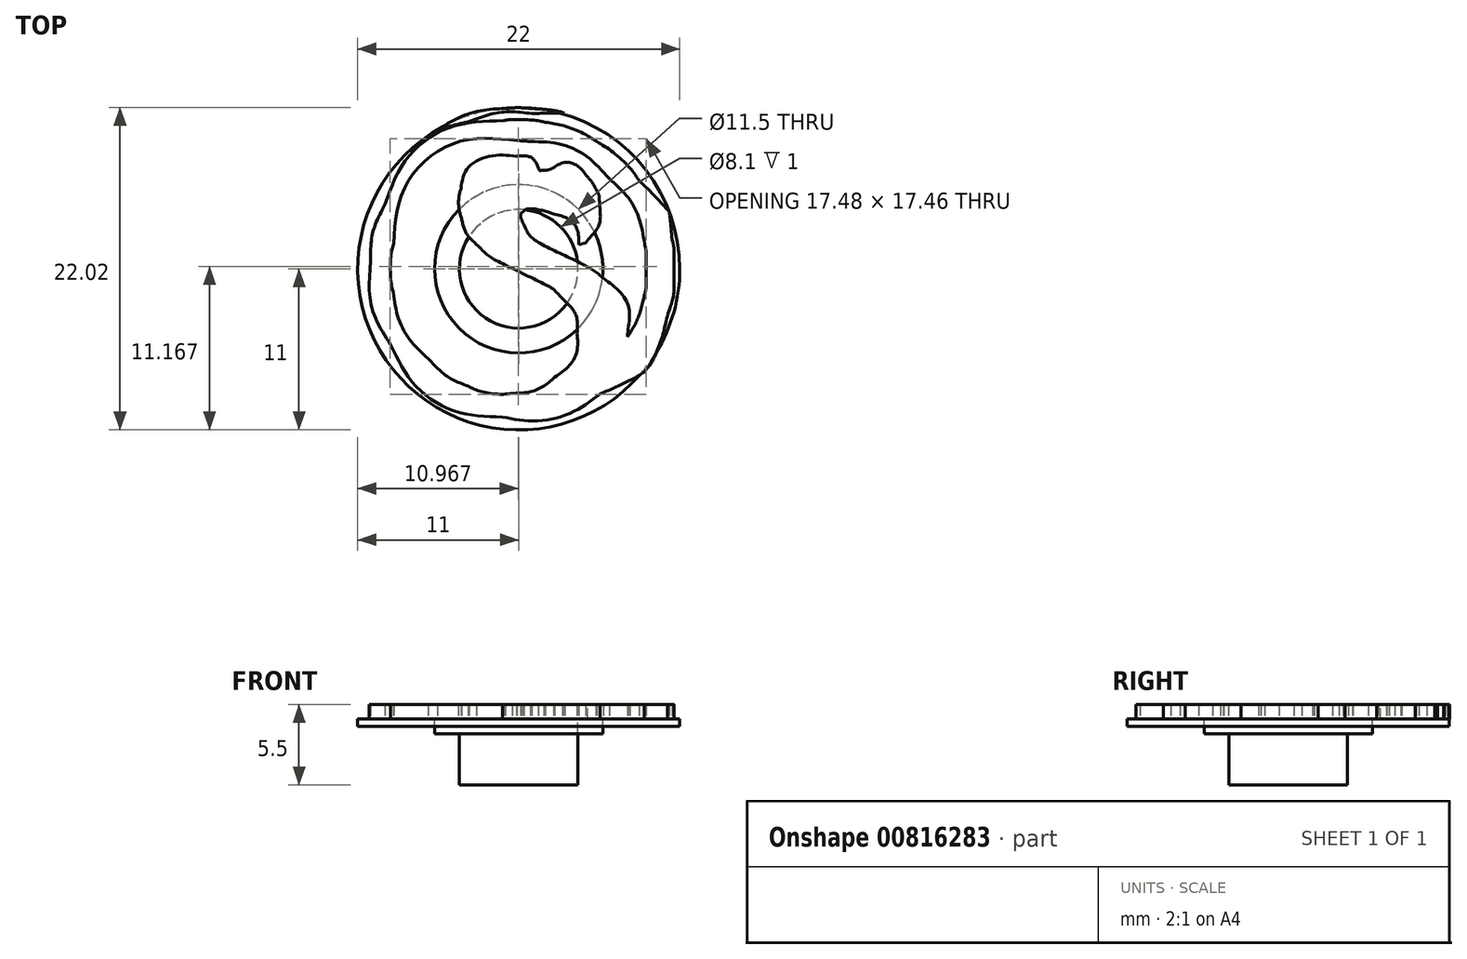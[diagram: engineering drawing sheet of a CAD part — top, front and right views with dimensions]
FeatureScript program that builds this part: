
annotation { "Feature Type Name" : "Feature", "Feature Type Description" : "" }
export const myFeature = defineFeature(function(context is Context, id is Id, definition is map)
    precondition{}
    {
        {
            var Q0;
            Q0=qCreatedBy(makeId("Top.planeOp"),FACE);
            var sketch = newSketch(context, id + "F0", { "sketchPlane" : qUnion([Q0])});
            skCircle(sketch, "E0", {"center": v(0, 0) * mm, "radius": 4.05 * mm});
            skCircle(sketch, "E1", {"center": v(0, 0) * mm, "radius": 5.75 * mm});
            skCircle(sketch, "E2", {"center": v(0, 0) * mm, "radius": 11 * mm});
            skSolve(sketch);
        }
        {
            var Q0;
            Q0=makeQuery(id+"F0.imprint","IMPRINT",FACE,{"disambiguationData":[TD([[makeQuery(id+"F0.imprint","IMPRINT",EDGE,{"derivedFrom":sQuery(id+"F0.wireOp",EDGE,"E0")}),-1.0]])]});
            extrude(context, id + "F1", {"entities" : qUnion([Q0]), "oppositeDirection" : true, "depth" : 1 * mm, "offsetDistance" : 25 * mm});
        }
        {
            var Q0;
            Q0=makeQuery(id+"F0.imprint","IMPRINT",FACE,{"disambiguationData":[TD([[makeQuery(id+"F0.imprint","IMPRINT",EDGE,{"derivedFrom":sQuery(id+"F0.wireOp",EDGE,"E1")}),-1.0]])]});
            extrude(context, id + "F2", {"entities" : qUnion([Q0]), "oppositeDirection" : true, "depth" : 0.5 * mm, "offsetDistance" : 25 * mm});
        }
        {
            var Q0;
            Q0=makeQuery(id+"F0.imprint","IMPRINT",FACE,{"disambiguationData":[TD([[makeQuery(id+"F0.imprint","IMPRINT",EDGE,{"derivedFrom":sQuery(id+"F0.wireOp",EDGE,"E0")}),1.0]])]});
            extrude(context, id + "F3", {"entities" : qUnion([Q0]), "oppositeDirection" : true, "depth" : 4.5 * mm, "offsetDistance" : 25 * mm});
        }
        {
            var Q0;
            Q0=makeQuery(id+"F3.opExtrude","CAP_FACE",FACE,{"disambiguationData":[OSD([sQuery(id+"F0.wireOp",EDGE,"E0")])],"isStart":true});
            var sketch = newSketch(context, id + "F4", { "sketchPlane" : qUnion([Q0])});
            skLineSegment(sketch, "E3", {"start": v(7.56, -4.44) * mm, "end": v(7.44, -4.63) * mm});
            skLineSegment(sketch, "E4", {"start": v(7.44, -4.63) * mm, "end": v(7.47, -4.1) * mm});
            skLineSegment(sketch, "E5", {"start": v(7.47, -4.1) * mm, "end": v(7.56, -4.44) * mm});
            skLineSegment(sketch, "E6", {"start": v(4.1, 1.64) * mm, "end": v(4.14, 1.26) * mm});
            skLineSegment(sketch, "E7", {"start": v(4.14, 1.26) * mm, "end": v(4.57, 1.8) * mm});
            skLineSegment(sketch, "E8", {"start": v(4.57, 1.8) * mm, "end": v(4.1, 1.64) * mm});
            skFitSpline(sketch, "E9", {"points": [v(-0.93, 10.95) * mm, v(-2.51, 10.82) * mm, v(-4.2, 10.27) * mm, v(-5.56, 9.46) * mm]});
            skFitSpline(sketch, "E10", {"points": [v(-5.56, 9.46) * mm, v(-9.07, 7.36) * mm, v(-11.1, 3.62) * mm, v(-10.95, -0.42) * mm]});
            skFitSpline(sketch, "E11", {"points": [v(-10.95, -0.42) * mm, v(-10.91, -1.53) * mm, v(-10.75, -2.45) * mm, v(-10.4, -3.46) * mm]});
            skFitSpline(sketch, "E12", {"points": [v(-10.4, -3.46) * mm, v(-9.46, -6.32) * mm, v(-7.43, -8.62) * mm, v(-4.73, -9.92) * mm]});
            skFitSpline(sketch, "E13", {"points": [v(-4.73, -9.92) * mm, v(1.4, -12.85) * mm, v(8.7, -9.58) * mm, v(10.58, -3.04) * mm]});
            skFitSpline(sketch, "E14", {"points": [v(10.58, -3.04) * mm, v(10.9, -1.92) * mm, v(10.96, -1.5) * mm, v(10.96, 0.03) * mm]});
            skFitSpline(sketch, "E15", {"points": [v(10.96, 0.03) * mm, v(10.96, 1.31) * mm, v(10.95, 1.48) * mm, v(10.8, 2.17) * mm]});
            skFitSpline(sketch, "E16", {"points": [v(10.8, 2.17) * mm, v(10.07, 5.61) * mm, v(7.88, 8.4) * mm, v(4.75, 9.91) * mm]});
            skFitSpline(sketch, "E17", {"points": [v(4.75, 9.91) * mm, v(3.5, 10.5) * mm, v(2.3, 10.83) * mm, v(0.81, 10.95) * mm]});
            skFitSpline(sketch, "E18", {"points": [v(0.81, 10.95) * mm, v(-0.02, 11.02) * mm, v(-0.04, 11.02) * mm, v(-0.93, 10.95) * mm]});
            skFitSpline(sketch, "E19", {"points": [v(0.9, 10.6) * mm, v(5.64, 10.17) * mm, v(9.44, 6.78) * mm, v(10.47, 2.05) * mm]});
            skFitSpline(sketch, "E20", {"points": [v(10.47, 2.05) * mm, v(10.59, 1.5) * mm, v(10.6, 1.26) * mm, v(10.6, 0) * mm]});
            skFitSpline(sketch, "E21", {"points": [v(10.6, 0) * mm, v(10.6, -1.57) * mm, v(10.54, -2.01) * mm, v(10.15, -3.22) * mm]});
            skFitSpline(sketch, "E22", {"points": [v(10.15, -3.22) * mm, v(9.27, -6) * mm, v(7.28, -8.29) * mm, v(4.67, -9.56) * mm]});
            skFitSpline(sketch, "E23", {"points": [v(4.67, -9.56) * mm, v(0.18, -11.76) * mm, v(-5.17, -10.54) * mm, v(-8.3, -6.61) * mm]});
            skFitSpline(sketch, "E24", {"points": [v(-8.3, -6.61) * mm, v(-9.36, -5.3) * mm, v(-10.05, -3.8) * mm, v(-10.42, -2.06) * mm]});
            skFitSpline(sketch, "E25", {"points": [v(-10.42, -2.06) * mm, v(-10.56, -1.38) * mm, v(-10.58, -1.18) * mm, v(-10.58, -0.06) * mm]});
            skFitSpline(sketch, "E26", {"points": [v(-10.58, -0.06) * mm, v(-10.59, 1.28) * mm, v(-10.5, 1.87) * mm, v(-10.22, 2.88) * mm]});
            skFitSpline(sketch, "E27", {"points": [v(-10.22, 2.88) * mm, v(-9.25, 6.26) * mm, v(-6.7, 8.93) * mm, v(-3.4, 10.06) * mm]});
            skFitSpline(sketch, "E28", {"points": [v(-3.4, 10.06) * mm, v(-1.94, 10.55) * mm, v(-0.57, 10.73) * mm, v(0.9, 10.6) * mm]});
            skFitSpline(sketch, "E29", {"points": [v(-1.06, 10.12) * mm, v(-4.64, 9.68) * mm, v(-7.6, 7.58) * mm, v(-9.14, 4.4) * mm]});
            skFitSpline(sketch, "E30", {"points": [v(-9.14, 4.4) * mm, v(-9.8, 3.03) * mm, v(-10.07, 1.91) * mm, v(-10.12, 0.4) * mm]});
            skFitSpline(sketch, "E31", {"points": [v(-10.12, 0.4) * mm, v(-10.2, -1.68) * mm, v(-9.76, -3.44) * mm, v(-8.75, -5.17) * mm]});
            skFitSpline(sketch, "E32", {"points": [v(-8.75, -5.17) * mm, v(-7.14, -7.9) * mm, v(-4.33, -9.72) * mm, v(-1.12, -10.12) * mm]});
            skFitSpline(sketch, "E33", {"points": [v(-1.12, -10.12) * mm, v(1.12, -10.4) * mm, v(3.64, -9.8) * mm, v(5.56, -8.54) * mm]});
            skFitSpline(sketch, "E34", {"points": [v(5.56, -8.54) * mm, v(10.48, -5.3) * mm, v(11.68, 1.27) * mm, v(8.21, 6.02) * mm]});
            skFitSpline(sketch, "E35", {"points": [v(8.21, 6.02) * mm, v(7.55, 6.93) * mm, v(6.34, 8.04) * mm, v(5.32, 8.68) * mm]});
            skFitSpline(sketch, "E36", {"points": [v(5.32, 8.68) * mm, v(4.4, 9.26) * mm, v(3, 9.79) * mm, v(1.82, 10) * mm]});
            skFitSpline(sketch, "E37", {"points": [v(1.82, 10) * mm, v(1.07, 10.14) * mm, v(-0.39, 10.2) * mm, v(-1.06, 10.12) * mm]});
            skFitSpline(sketch, "E38", {"points": [v(0.81, 8.7) * mm, v(2.87, 8.5) * mm, v(4.7, 7.64) * mm, v(6.2, 6.15) * mm]});
            skFitSpline(sketch, "E39", {"points": [v(6.2, 6.15) * mm, v(7.45, 4.88) * mm, v(8.21, 3.48) * mm, v(8.6, 1.68) * mm]});
            skFitSpline(sketch, "E40", {"points": [v(8.6, 1.68) * mm, v(8.68, 1.3) * mm, v(8.7, 0.92) * mm, v(8.7, -0.06) * mm]});
            skFitSpline(sketch, "E41", {"points": [v(8.7, -0.06) * mm, v(8.7, -1.17) * mm, v(8.69, -1.37) * mm, v(8.56, -1.87) * mm]});
            skFitSpline(sketch, "E42", {"points": [v(8.56, -1.87) * mm, v(8.32, -2.85) * mm, v(7.97, -3.76) * mm, v(7.56, -4.44) * mm]});
            skFitSpline(sketch, "E43", {"points": [v(7.47, -4.1) * mm, v(7.55, -2.8) * mm, v(6.99, -1.66) * mm, v(5.77, -0.65) * mm]});
            skFitSpline(sketch, "E44", {"points": [v(5.77, -0.65) * mm, v(5.23, -0.2) * mm, v(4.43, 0.28) * mm, v(3.16, 0.9) * mm]});
            skFitSpline(sketch, "E45", {"points": [v(3.16, 0.9) * mm, v(1.55, 1.7) * mm, v(0.71, 2.33) * mm, v(0.37, 3) * mm]});
            skFitSpline(sketch, "E46", {"points": [v(0.37, 3) * mm, v(0.18, 3.4) * mm, v(0.14, 3.77) * mm, v(0.27, 3.88) * mm]});
            skFitSpline(sketch, "E47", {"points": [v(0.27, 3.88) * mm, v(0.5, 4.08) * mm, v(1.54, 4) * mm, v(2.4, 3.73) * mm]});
            skFitSpline(sketch, "E48", {"points": [v(2.4, 3.73) * mm, v(3.38, 3.42) * mm, v(4, 2.68) * mm, v(4.1, 1.64) * mm]});
            skFitSpline(sketch, "E49", {"points": [v(4.57, 1.8) * mm, v(5.34, 2.72) * mm, v(5.57, 3.34) * mm, v(5.52, 4.4) * mm]});
            skFitSpline(sketch, "E50", {"points": [v(5.52, 4.4) * mm, v(5.5, 4.96) * mm, v(5.47, 5.05) * mm, v(5.28, 5.45) * mm]});
            skFitSpline(sketch, "E51", {"points": [v(5.28, 5.45) * mm, v(5.15, 5.7) * mm, v(4.9, 6.05) * mm, v(4.7, 6.28) * mm]});
            skFitSpline(sketch, "E52", {"points": [v(4.7, 6.28) * mm, v(4, 7.04) * mm, v(3.16, 7.27) * mm, v(2.37, 6.9) * mm]});
            skFitSpline(sketch, "E53", {"points": [v(2.37, 6.9) * mm, v(2.18, 6.81) * mm, v(1.9, 6.74) * mm, v(1.73, 6.73) * mm]});
            skFitSpline(sketch, "E54", {"points": [v(1.73, 6.73) * mm, v(1.44, 6.71) * mm, v(1.42, 6.72) * mm, v(1.33, 6.9) * mm]});
            skFitSpline(sketch, "E55", {"points": [v(1.33, 6.9) * mm, v(1.05, 7.45) * mm, v(0.58, 7.7) * mm, v(-0.15, 7.7) * mm]});
            skFitSpline(sketch, "E56", {"points": [v(-0.15, 7.7) * mm, v(-2.06, 7.68) * mm, v(-3.55, 6.8) * mm, v(-3.94, 5.45) * mm]});
            skFitSpline(sketch, "E57", {"points": [v(-3.94, 5.45) * mm, v(-4.09, 4.97) * mm, v(-4.07, 4.06) * mm, v(-3.91, 3.45) * mm]});
            skFitSpline(sketch, "E58", {"points": [v(-3.91, 3.45) * mm, v(-3.72, 2.74) * mm, v(-3.42, 2.2) * mm, v(-2.87, 1.66) * mm]});
            skFitSpline(sketch, "E59", {"points": [v(-2.87, 1.66) * mm, v(-2.22, 1) * mm, v(-1.52, 0.57) * mm, v(0.25, -0.3) * mm]});
            skFitSpline(sketch, "E60", {"points": [v(0.25, -0.3) * mm, v(2, -1.17) * mm, v(2.4, -1.43) * mm, v(3, -2.04) * mm]});
            skFitSpline(sketch, "E61", {"points": [v(3, -2.04) * mm, v(3.7, -2.79) * mm, v(3.99, -3.47) * mm, v(3.99, -4.41) * mm]});
            skFitSpline(sketch, "E62", {"points": [v(3.99, -4.41) * mm, v(3.99, -5.59) * mm, v(3.47, -6.6) * mm, v(2.46, -7.4) * mm]});
            skFitSpline(sketch, "E63", {"points": [v(2.46, -7.4) * mm, v(1.64, -8.05) * mm, v(0.67, -8.42) * mm, v(-0.43, -8.5) * mm]});
            skFitSpline(sketch, "E64", {"points": [v(-0.43, -8.5) * mm, v(-1.35, -8.56) * mm, v(-2.67, -8.35) * mm, v(-3.45, -8.02) * mm]});
            skFitSpline(sketch, "E65", {"points": [v(-3.45, -8.02) * mm, v(-4.5, -7.56) * mm, v(-5.32, -7) * mm, v(-6.2, -6.12) * mm]});
            skFitSpline(sketch, "E66", {"points": [v(-6.2, -6.12) * mm, v(-7.42, -4.89) * mm, v(-8.22, -3.36) * mm, v(-8.58, -1.6) * mm]});
            skFitSpline(sketch, "E67", {"points": [v(-8.58, -1.6) * mm, v(-8.74, -0.8) * mm, v(-8.73, 0.91) * mm, v(-8.55, 1.73) * mm]});
            skFitSpline(sketch, "E68", {"points": [v(-8.55, 1.73) * mm, v(-7.67, 5.79) * mm, v(-4.26, 8.62) * mm, v(-0.1, 8.75) * mm]});
            skFitSpline(sketch, "E69", {"points": [v(-0.1, 8.75) * mm, v(0.04, 8.75) * mm, v(0.46, 8.73) * mm, v(0.81, 8.7) * mm]});
            skFitSpline(sketch, "E70", {"points": [v(-7.18, -0.9) * mm, v(-7.67, -0.93) * mm, v(-7.65, -0.9) * mm, v(-7.46, -1.8) * mm]});
            skFitSpline(sketch, "E71", {"points": [v(-7.46, -1.8) * mm, v(-6.76, -5.1) * mm, v(-3.86, -7.57) * mm, v(-0.68, -7.58) * mm]});
            skFitSpline(sketch, "E72", {"points": [v(-0.68, -7.58) * mm, v(0.73, -7.59) * mm, v(1.55, -7.17) * mm, v(2.04, -6.16) * mm]});
            skFitSpline(sketch, "E73", {"points": [v(2.04, -6.16) * mm, v(2.23, -5.78) * mm, v(2.24, -5.73) * mm, v(2.24, -5.08) * mm]});
            skFitSpline(sketch, "E74", {"points": [v(2.24, -5.08) * mm, v(2.24, -4.44) * mm, v(2.22, -4.37) * mm, v(2.05, -4) * mm]});
            skFitSpline(sketch, "E75", {"points": [v(2.05, -4) * mm, v(1.66, -3.18) * mm, v(0.97, -2.56) * mm, v(-0.14, -2.02) * mm]});
            skFitSpline(sketch, "E76", {"points": [v(-0.14, -2.02) * mm, v(-1.14, -1.53) * mm, v(-2.26, -1.2) * mm, v(-3.56, -1) * mm]});
            skFitSpline(sketch, "E77", {"points": [v(-3.56, -1) * mm, v(-4.17, -0.92) * mm, v(-6.38, -0.85) * mm, v(-7.18, -0.9) * mm]});
            skSolve(sketch);
        }
        {
            var Q0;
            Q0=makeQuery(id+"F4.imprint","IMPRINT",FACE,{"disambiguationData":[TD([[makeQuery(id+"F4.imprint","IMPRINT",EDGE,{"derivedFrom":sQuery(id+"F4.wireOp",EDGE,"E8")}),-1.0]])]});
            var Q1;
            {var subQ4=sQuery(id+"F4.wireOp",EDGE,"E45");Q1=makeQuery(id+"F4.imprint","IMPRINT",FACE,{"disambiguationData":[TD([[makeQuery(id+"F4.imprint","IMPRINT",EDGE,{"derivedFrom":subQ4}),1.0]])]});}
            var Q2;
            Q2=makeQuery(id+"F4.imprint","IMPRINT",FACE,{"disambiguationData":[TD([[makeQuery(id+"F4.imprint","IMPRINT",EDGE,{"derivedFrom":sQuery(id+"F4.wireOp",EDGE,"E3")}),1.0]])]});
            var Q3;
            Q3=makeQuery(id+"F4.imprint","IMPRINT",FACE,{"disambiguationData":[TD([[makeQuery(id+"F4.imprint","IMPRINT",EDGE,{"derivedFrom":sQuery(id+"F4.wireOp",EDGE,"E9")}),1.0]])]});
            extrude(context, id + "F5", {"entities" : qUnion([Q0, Q1, Q2, Q3]), "depth" : 1 * mm, "offsetDistance" : 25 * mm});
        }
    });
